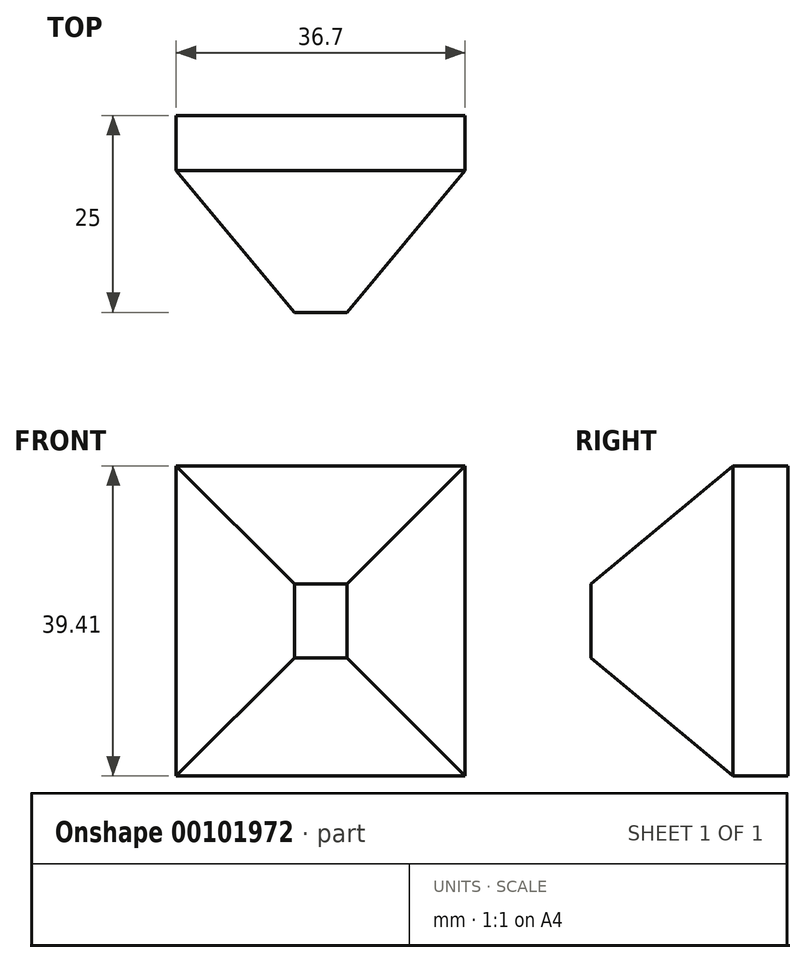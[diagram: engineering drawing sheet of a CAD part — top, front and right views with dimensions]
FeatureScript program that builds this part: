
annotation { "Feature Type Name" : "Feature", "Feature Type Description" : "" }
export const myFeature = defineFeature(function(context is Context, id is Id, definition is map)
    precondition{}
    {
        {
            var Q0;
            Q0=qCreatedBy(makeId("Front.planeOp"),FACE);
            var sketch = newSketch(context, id + "F0", { "sketchPlane" : qUnion([Q0])});
            skLineSegment(sketch, "E0.bottom", {"start": v(0, -4.36) * mm, "end": v(-36.7, -4.36) * mm});
            skLineSegment(sketch, "E0.top", {"start": v(0, 35.05) * mm, "end": v(-36.7, 35.05) * mm});
            skLineSegment(sketch, "E0.left", {"start": v(0, -4.36) * mm, "end": v(0, 35.05) * mm});
            skLineSegment(sketch, "E0.right", {"start": v(-36.7, -4.36) * mm, "end": v(-36.7, 35.05) * mm});
            skSolve(sketch);
        }
        {
            var Q0;
            Q0 = qSketchRegion(id + "F0", true);
            extrude(context, id + "F1", {"entities" : qUnion([Q0]), "depth" : 25 * mm});
        }
        {
            var Q0;
            Q0=makeQuery(id+"F1.opExtrude","CAP_FACE",FACE,{"disambiguationData":[OSD([sQuery(id+"F0.wireOp",EDGE,"E0.bottom"),sQuery(id+"F0.wireOp",EDGE,"E0.top"),sQuery(id+"F0.wireOp",EDGE,"E0.left"),sQuery(id+"F0.wireOp",EDGE,"E0.right")])],"isStart":false});
            chamfer(context, id + "F2", {"entities" : qUnion([Q0]), "chamferType" : ChamferType.TWO_OFFSETS, "width1" : 18 * mm, "oppositeDirection" : false, "width2" : 15 * mm, "tangentPropagation" : true});
        }
    });
